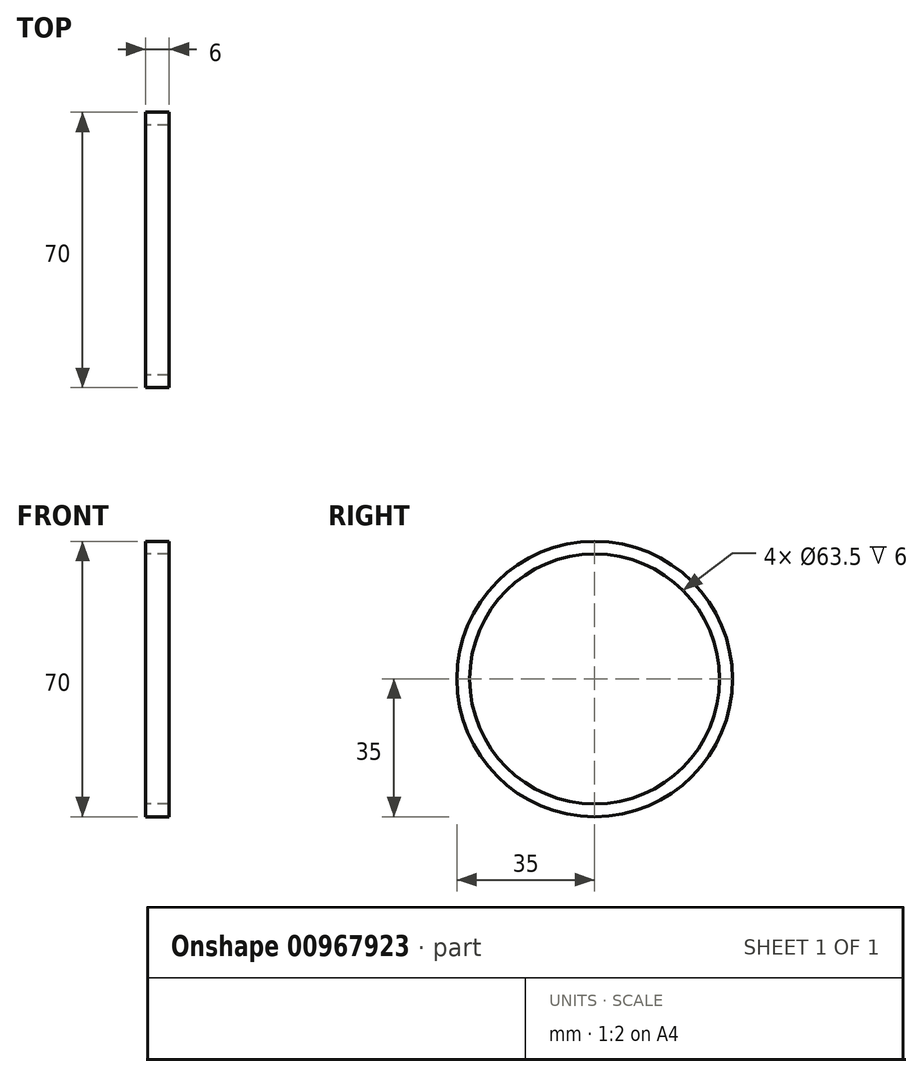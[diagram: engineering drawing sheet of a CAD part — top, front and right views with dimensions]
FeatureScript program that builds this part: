
annotation { "Feature Type Name" : "Feature", "Feature Type Description" : "" }
export const myFeature = defineFeature(function(context is Context, id is Id, definition is map)
    precondition{}
    {
        {
            var Q0;
            Q0=qCreatedBy(makeId("Right.planeOp"),FACE);
            var sketch = newSketch(context, id + "F0", { "sketchPlane" : qUnion([Q0])});
            skCircle(sketch, "E0", {"center": v(0, 0) * mm, "radius": 35 * mm});
            skCircle(sketch, "E1", {"center": v(0, 0) * mm, "radius": 31.75 * mm});
            skSolve(sketch);
        }
        {
            var Q0;
            Q0=makeQuery(id+"F0.imprint","IMPRINT",FACE,{"disambiguationData":[TD([[makeQuery(id+"F0.imprint","IMPRINT",EDGE,{"derivedFrom":sQuery(id+"F0.wireOp",EDGE,"E0")}),1.0]])]});
            extrude(context, id + "F1", {"entities" : qUnion([Q0]), "depth" : 6 * mm, "offsetDistance" : 25 * mm});
        }
    });
